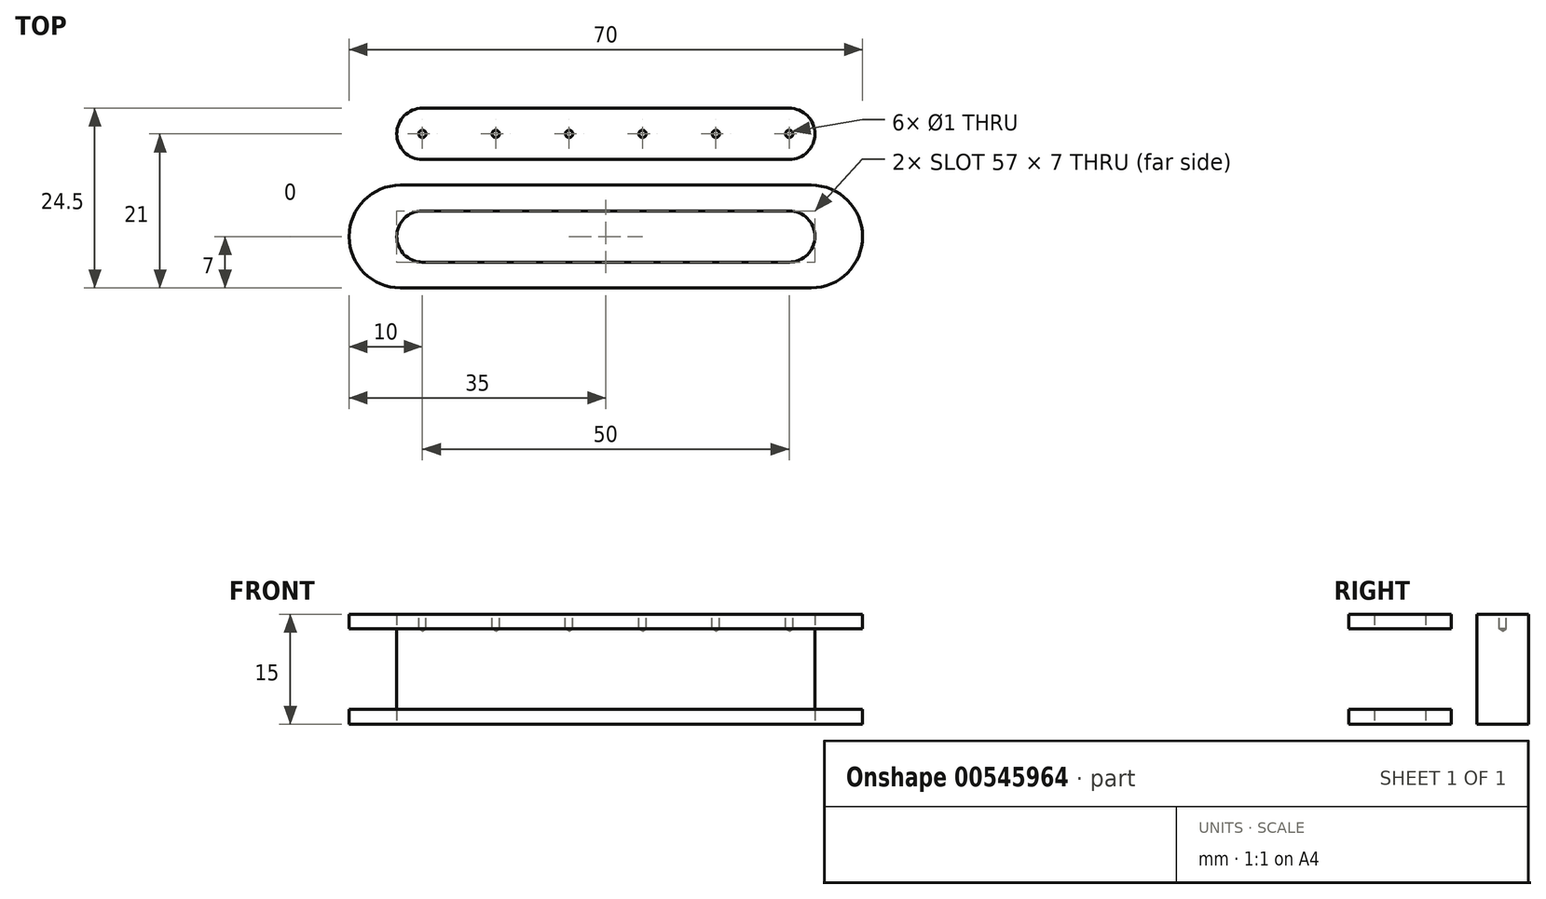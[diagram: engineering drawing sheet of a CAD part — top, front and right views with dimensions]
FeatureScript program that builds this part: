
annotation { "Feature Type Name" : "Feature", "Feature Type Description" : "" }
export const myFeature = defineFeature(function(context is Context, id is Id, definition is map)
    precondition{}
    {
        {
            var Q0;
            Q0=qCreatedBy(makeId("Top.planeOp"),FACE);
            var sketch = newSketch(context, id + "F0", { "sketchPlane" : qUnion([Q0])});
            skLineSegment(sketch, "E0.bottom", {"start": v(28, -7) * mm, "end": v(-28, -7) * mm});
            skLineSegment(sketch, "E0.top", {"start": v(28, 7) * mm, "end": v(-28, 7) * mm});
            skLineSegment(sketch, "E0.left", {"start": v(35, 0) * mm, "end": v(35, 0) * mm});
            skLineSegment(sketch, "E0.right", {"start": v(-35, 0) * mm, "end": v(-35, 0) * mm});
            skPoint(sketch, "E0.middle", {"position": v(0, 0) * mm});
            skPoint(sketch, "E1.visualSharp", {"position": v(-35, 7) * mm});
            skArc(sketch, "E1.filletArc", {"start": v(-28, 7) * mm, "mid": v(-32.95, 4.95) * mm, "end": v(-35, 0) * mm});
            skPoint(sketch, "E2.visualSharp", {"position": v(-35, -7) * mm});
            skArc(sketch, "E2.filletArc", {"start": v(-35, 0) * mm, "mid": v(-32.95, -4.95) * mm, "end": v(-28, -7) * mm});
            skPoint(sketch, "E3.visualSharp", {"position": v(35, 7) * mm});
            skArc(sketch, "E3.filletArc", {"start": v(35, 0) * mm, "mid": v(32.95, 4.95) * mm, "end": v(28, 7) * mm});
            skPoint(sketch, "E4.visualSharp", {"position": v(35, -7) * mm});
            skArc(sketch, "E4.filletArc", {"start": v(28, -7) * mm, "mid": v(32.95, -4.95) * mm, "end": v(35, 0) * mm});
            skPoint(sketch, "E5", {"position": v(15, 0) * mm});
            skPoint(sketch, "E6", {"position": v(5, 0) * mm});
            skPoint(sketch, "E7", {"position": v(-5, 0) * mm});
            skPoint(sketch, "E8", {"position": v(-15, 0) * mm});
            skPoint(sketch, "E9", {"position": v(-25, 0) * mm});
            skPoint(sketch, "E10", {"position": v(25, 0) * mm});
            skLineSegment(sketch, "E11.bottom", {"start": v(25, 3.5) * mm, "end": v(-25, 3.5) * mm});
            skLineSegment(sketch, "E11.top", {"start": v(25, -3.5) * mm, "end": v(-25, -3.5) * mm});
            skLineSegment(sketch, "E11.left", {"start": v(28.5, 0) * mm, "end": v(28.5, 0) * mm});
            skLineSegment(sketch, "E11.right", {"start": v(-28.5, 0) * mm, "end": v(-28.5, 0) * mm});
            skPoint(sketch, "E12.visualSharp", {"position": v(-28.5, 3.5) * mm});
            skArc(sketch, "E12.filletArc", {"start": v(-25, 3.5) * mm, "mid": v(-27.47, 2.47) * mm, "end": v(-28.5, 0) * mm});
            skPoint(sketch, "E13.visualSharp", {"position": v(-28.5, -3.5) * mm});
            skArc(sketch, "E13.filletArc", {"start": v(-28.5, 0) * mm, "mid": v(-27.47, -2.47) * mm, "end": v(-25, -3.5) * mm});
            skPoint(sketch, "E14.visualSharp", {"position": v(28.5, -3.5) * mm});
            skArc(sketch, "E14.filletArc", {"start": v(25, -3.5) * mm, "mid": v(27.47, -2.47) * mm, "end": v(28.5, 0) * mm});
            skPoint(sketch, "E15.visualSharp", {"position": v(28.5, 3.5) * mm});
            skArc(sketch, "E15.filletArc", {"start": v(28.5, 0) * mm, "mid": v(27.47, 2.47) * mm, "end": v(25, 3.5) * mm});
            skSolve(sketch);
        }
        {
            var Q0;
            Q0=makeQuery(id+"F0.imprint","IMPRINT",FACE,{"disambiguationData":[TD([[makeQuery(id+"F0.imprint","IMPRINT",EDGE,{"derivedFrom":sQuery(id+"F0.wireOp",EDGE,"E11.bottom")}),1.0]])]});
            extrude(context, id + "F1", {"entities" : qUnion([Q0]), "depth" : 15 * mm, "offsetDistance" : 25 * mm});
        }
        {
            var Q0;
            Q0 = qSketchRegion(id + "F0", true);
            extrude(context, id + "F2", {"entities" : qUnion([Q0]), "depth" : 2 * mm, "offsetDistance" : 25 * mm});
        }
        {
            var Q0;
            Q0=makeQuery(id+"F2.opExtrude","SWEPT_BODY",BODY,{"disambiguationData":[OSD([sQuery(id+"F0.wireOp",EDGE,"E0.bottom"),sQuery(id+"F0.wireOp",EDGE,"E0.top"),sQuery(id+"F0.wireOp",EDGE,"E1.filletArc"),sQuery(id+"F0.wireOp",EDGE,"E2.filletArc"),sQuery(id+"F0.wireOp",EDGE,"E3.filletArc"),sQuery(id+"F0.wireOp",EDGE,"E4.filletArc"),sQuery(id+"F0.wireOp",EDGE,"E11.bottom"),sQuery(id+"F0.wireOp",EDGE,"E11.top"),sQuery(id+"F0.wireOp",EDGE,"E12.filletArc"),sQuery(id+"F0.wireOp",EDGE,"E13.filletArc"),sQuery(id+"F0.wireOp",EDGE,"E14.filletArc"),sQuery(id+"F0.wireOp",EDGE,"E15.filletArc")])]});
            var Q1;
            Q1=makeQuery(id+"F1.opExtrude","SWEPT_EDGE",EDGE,{"disambiguationData":[OSD([sQuery(id+"F0.wireOp",EDGE,"E11.bottom"),sQuery(id+"F0.wireOp",EDGE,"E12.filletArc")])]});
            transform(context, id + "F3", {"entities" : qUnion([Q0]), "transformType" : TransformType.TRANSLATION_DISTANCE, "transformDirection" : qUnion([Q1]), "distance" : 13 * mm, "oppositeDirection" : true, "makeCopy" : true});
        }
        {
            var Q0;
            Q0=sQuery(id+"F0.wireOp",VERTEX,"E9");
            var Q1;
            Q1=sQuery(id+"F0.wireOp",VERTEX,"E8");
            var Q2;
            Q2=sQuery(id+"F0.wireOp",VERTEX,"E7");
            var Q3;
            Q3=sQuery(id+"F0.wireOp",VERTEX,"E6");
            var Q4;
            Q4=sQuery(id+"F0.wireOp",VERTEX,"E5");
            var Q5;
            Q5=sQuery(id+"F0.wireOp",VERTEX,"E10");
            var Q6;
            Q6=makeQuery(id+"F1.opExtrude","SWEPT_BODY",BODY,{"disambiguationData":[OSD([sQuery(id+"F0.wireOp",EDGE,"E11.bottom"),sQuery(id+"F0.wireOp",EDGE,"E11.top"),sQuery(id+"F0.wireOp",EDGE,"E12.filletArc"),sQuery(id+"F0.wireOp",EDGE,"E13.filletArc"),sQuery(id+"F0.wireOp",EDGE,"E14.filletArc"),sQuery(id+"F0.wireOp",EDGE,"E15.filletArc")])]});
            hole(context, id + "F4", {"style" : HoleStyle.SIMPLE, "endStyle" : HoleEndStyle.BLIND, "oppositeDirection" : true, "holeDiameter" : 1 * mm, "holeDepth" : 2 * mm, "isTappedThrough" : true, "tappedDepth" : 12 * mm, "tapClearance" : 3, "startFromSketch" : true, "locations" : qUnion([Q0, Q1, Q2, Q3, Q4, Q5]), "scope" : qUnion([Q6])});
        }
        {
            var Q0;
            Q0=makeQuery(id+"F1.opExtrude","SWEPT_BODY",BODY,{"disambiguationData":[OSD([sQuery(id+"F0.wireOp",EDGE,"E11.bottom"),sQuery(id+"F0.wireOp",EDGE,"E11.top"),sQuery(id+"F0.wireOp",EDGE,"E12.filletArc"),sQuery(id+"F0.wireOp",EDGE,"E13.filletArc"),sQuery(id+"F0.wireOp",EDGE,"E14.filletArc"),sQuery(id+"F0.wireOp",EDGE,"E15.filletArc")])]});
            var Q1;
            Q1=makeQuery(id+"F2.opExtrude","CAP_EDGE",EDGE,{"disambiguationData":[OSD([sQuery(id+"F0.wireOp",EDGE,"E0.top")])],"isStart":false});
            transform(context, id + "F5", {"entities" : qUnion([Q0]), "transformType" : TransformType.ROTATION, "transformAxis" : qUnion([Q1]), "angle" : 180 * degree, "makeCopy" : false});
        }
        {
            var Q0;
            Q0=makeQuery(id+"F1.opExtrude","SWEPT_BODY",BODY,{"disambiguationData":[OSD([sQuery(id+"F0.wireOp",EDGE,"E11.bottom"),sQuery(id+"F0.wireOp",EDGE,"E11.top"),sQuery(id+"F0.wireOp",EDGE,"E12.filletArc"),sQuery(id+"F0.wireOp",EDGE,"E13.filletArc"),sQuery(id+"F0.wireOp",EDGE,"E14.filletArc"),sQuery(id+"F0.wireOp",EDGE,"E15.filletArc")])]});
            var Q1;
            Q1=makeQuery(id+"F1.opExtrude","SWEPT_EDGE",EDGE,{"disambiguationData":[OSD([sQuery(id+"F0.wireOp",EDGE,"E11.bottom"),sQuery(id+"F0.wireOp",EDGE,"E12.filletArc")])]});
            transform(context, id + "F6", {"entities" : qUnion([Q0]), "transformType" : TransformType.TRANSLATION_DISTANCE, "transformDirection" : qUnion([Q1]), "distance" : 11 * mm, "makeCopy" : false});
        }
    });
